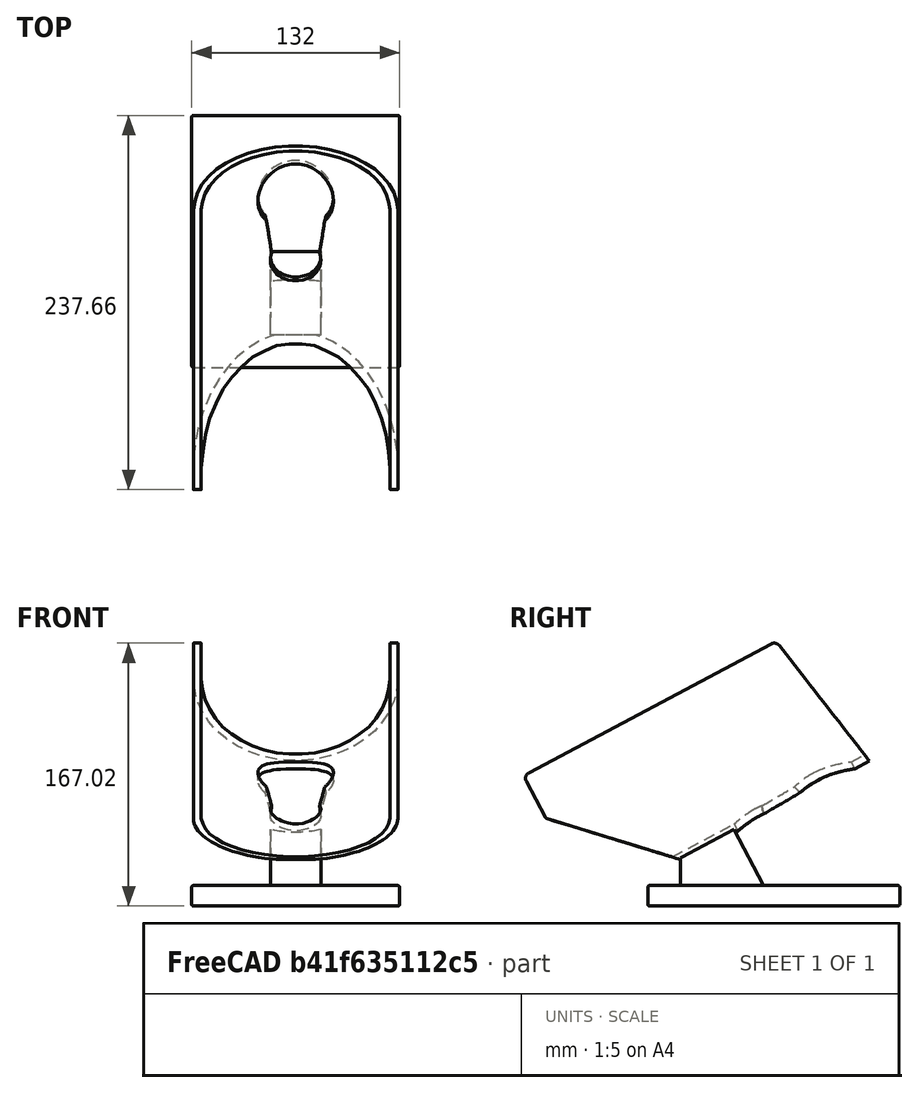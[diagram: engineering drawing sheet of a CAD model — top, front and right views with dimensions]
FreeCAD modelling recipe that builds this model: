
FCSTD DOCUMENT  (FreeCAD 0.16R6707 (Git))
Label: Calzador
License: All rights reserved
LicenseURL: http://en.wikipedia.org/wiki/All_rights_reserved
objects: Part::Cut×7, Part::Box×6, Part::Cylinder×4, Part::MultiFuse×4, Part::Fillet×3, Part::RuledSurface×2, Part::Extrusion×2, Part::Fuse×1, Part::Cone×1
note: 30 computed .brp shape members not serialized (recipe doc carries the construction recipe); baked Part::Feature solids carry a one-line shape summary decoded from their .brp

FEATURE [Part::Cylinder] Cylinder  label="Cilindro"
  Angle = 180
  Height = 200
  Radius = 65
FEATURE [Part::Cylinder] Cylinder001  label="Cilindro001"
  Angle = 360
  Height = 200
  Radius = 60
FEATURE [Part::Cut] Cut
  Base = -> Cylinder
  Tool = -> Cylinder001
FEATURE [Part::RuledSurface] Ruled_Surface
  Curve1 = -> Cut [Edge2]
  Curve2 = -> Cut [Edge9]
  Orientation = 0
FEATURE [Part::RuledSurface] Ruled_Surface001
  Curve1 = -> Cut [Edge4]
  Curve2 = -> Cut [Edge12]
  Orientation = 0
FEATURE [Part::Extrusion] Extrude
  Base = -> Ruled_Surface
  Dir = (0,-30,0)
  Solid = false
FEATURE [Part::Extrusion] Extrude001
  Base = -> Ruled_Surface001
  Dir = (0,-30,0)
  Solid = false
FEATURE [Part::Box] Box  label="Cubo"
  Height = 49
  Length = 132
  Placement = pos=(-66,20,-50) rot=(1,0,0;0.785398rad)
  Width = 122
FEATURE [Part::Fuse] Fusion
  Base = -> Cut
  Tool = -> Extrude001
FEATURE [Part::MultiFuse] Fusion001
  Shapes = -> [Extrude,Fusion]
FEATURE [Part::Cut] Cut001
  Base = -> Fusion001
  Tool = -> Box
FEATURE [Part::Box] Box001  label="Cubo001"
  Height = 26
  Length = 135
  Placement = pos=(-67,-40,180) rot=(1,0,0;0.174533rad)
  Width = 120
FEATURE [Part::Cut] Cut002
  Base = -> Cut001
  Tool = -> Box001
FEATURE [Part::Cylinder] Cylinder002  label="Cilindro002"
  Angle = 360
  Height = 20
  Placement = pos=(0,67,164) rot=(1,0,0;1.5708rad)
  Radius = 24
FEATURE [Part::Cut] Cut003
  Base = -> Cut002
  Tool = -> Cylinder002
FEATURE [Part::Cylinder] Cylinder003  label="Cilindro003"
  Angle = 360
  Height = 15
  Placement = pos=(0,70,120) rot=(1,0,0;1.5708rad)
  Radius = 16
FEATURE [Part::Cut] Cut004
  Base = -> Cut003
  Tool = -> Cylinder003
FEATURE [Part::Cone] Cone  label="Cono"
  Angle = 360
  Height = 35
  Placement = pos=(0,62,120) rot=(0,0,1;0rad)
  Radius1 = 15
  Radius2 = 20
FEATURE [Part::Cut] Cut005
  Base = -> Cut004
  Tool = -> Cone
FEATURE [Part::Box] Box002  label="Cubo002"
  Height = 37
  Length = 32
  Placement = pos=(-16,61,65) rot=(0,0,1;0rad)
  Width = 45
FEATURE [Part::Box] Box003  label="Cubo003"
  Height = 15
  Length = 132
  Placement = pos=(-66,82,30) rot=(1,0,0;1.0821rad)
  Width = 160
FEATURE [Part::MultiFuse] Fusion002
  Shapes = -> [Cut005,Box002]
FEATURE [Part::MultiFuse] Fusion003
  Shapes = -> [Fusion002,Box003]
FEATURE [Part::Box] Box004  label="Cubo004"
  Height = 7
  Length = 147
  Placement = pos=(-70,85,25) rot=(1,0,0;1.0821rad)
  Width = 175
FEATURE [Part::Cut] Cut006
  Base = -> Fusion003
  Tool = -> Box004
FEATURE [Part::Box] Box005  label="Cubo005"
  Height = 21
  Length = 32
  Placement = pos=(-16,79,55) rot=(1,0,0;1.0821rad)
  Width = 26
FEATURE [Part::MultiFuse] Fusion004
  Shapes = -> [Cut006,Box005]
FEATURE [Part::Fillet] Fillet
  Base = -> Fusion004
  Edges = 4 edges r=4: [Edge61,Edge65,Edge95,Edge99]
FEATURE [Part::Fillet] Fillet001
  Base = -> Fillet
  Edges = 2 edges r=1: [Edge66,Edge68]
FEATURE [Part::Fillet] Fillet002
  Base = -> Fillet001
  Edges = 12 edges r=1: [Edge104,Edge105,Edge106,Edge107,Edge110,Edge111,Edge112,Edge113,Edge114,Edge115,Edge116,Edge117]
  Placement = pos=(0,0,0) rot=(-1,0,0;1.0821rad)
